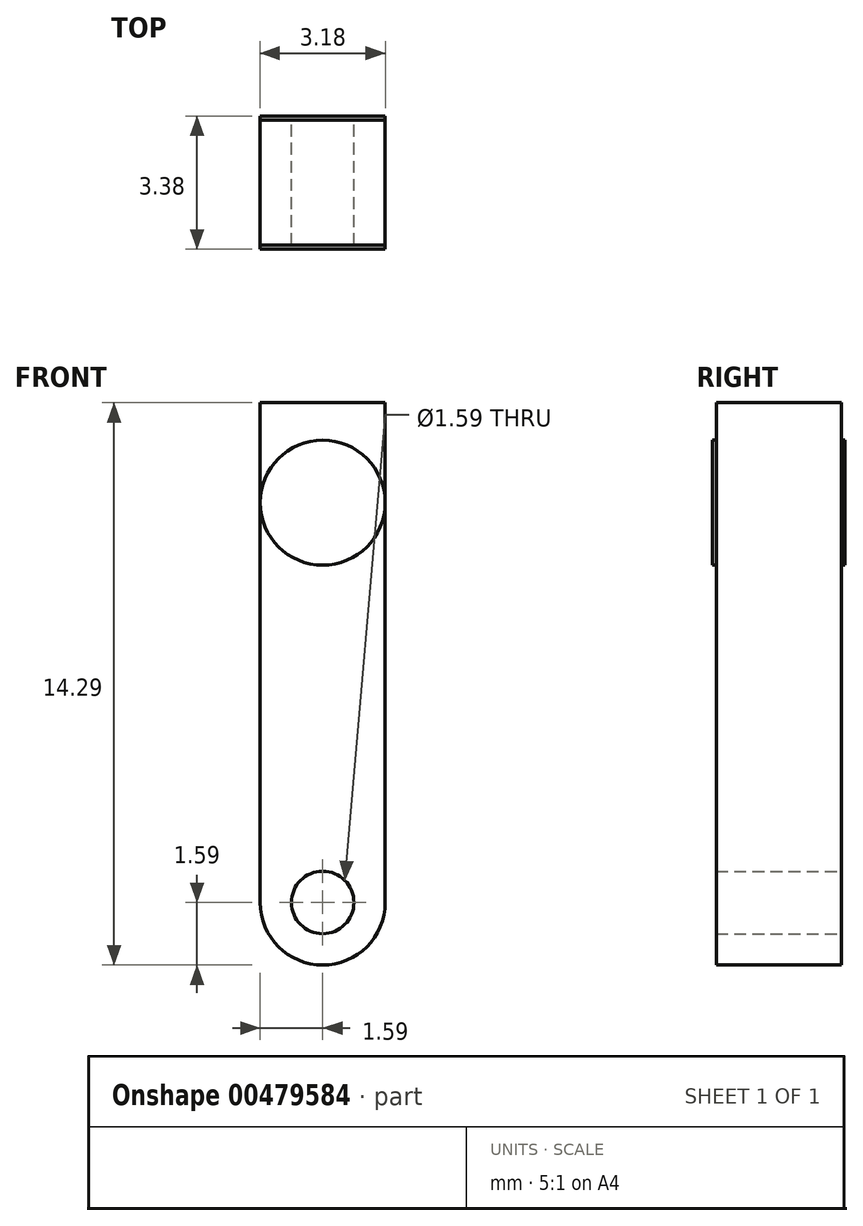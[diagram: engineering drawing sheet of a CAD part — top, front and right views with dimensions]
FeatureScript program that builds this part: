
annotation { "Feature Type Name" : "Feature", "Feature Type Description" : "" }
export const myFeature = defineFeature(function(context is Context, id is Id, definition is map)
    precondition{}
    {
        {
            var Q0;
            Q0=qCreatedBy(makeId("Front.planeOp"),FACE);
            var sketch = newSketch(context, id + "F0", { "sketchPlane" : qUnion([Q0])});
            skArc(sketch, "E0", {"start": v(-1.59, 0) * mm, "mid": v(0, -1.59) * mm, "end": v(1.59, 0) * mm});
            skLineSegment(sketch, "E1.bottom", {"start": v(-1.59, 0) * mm, "end": v(1.59, 0) * mm});
            skLineSegment(sketch, "E1.top", {"start": v(-1.59, 12.7) * mm, "end": v(1.59, 12.7) * mm});
            skLineSegment(sketch, "E1.left", {"start": v(-1.59, 0) * mm, "end": v(-1.59, 12.7) * mm});
            skLineSegment(sketch, "E1.right", {"start": v(1.59, 0) * mm, "end": v(1.59, 12.7) * mm});
            skCircle(sketch, "E2", {"center": v(0, 0) * mm, "radius": 0.8 * mm});
            skCircle(sketch, "E3", {"center": v(0, 10.16) * mm, "radius": 1.59 * mm});
            skSolve(sketch);
        }
        {
            var Q0;
            {var subQ1=sQuery(id+"F0.wireOp",EDGE,"E1.bottom");var subQ9=sQuery(id+"F0.wireOp",EDGE,"E2");var subQ11=makeQuery(id+"F0.imprint","INTERSECT",VERTEX,{"disambiguationData":[OD(0.0)],"derivedFrom":[subQ1,subQ9]});Q0=makeQuery(id+"F0.imprint","IMPRINT",FACE,{"disambiguationData":[TD([[makeQuery(id+"F0.imprint","IMPRINT",EDGE,{"disambiguationData":[TD([[subQ11,1.0]])],"derivedFrom":subQ9}),-1.0]])]});}
            var Q1;
            {var subQ0=sQuery(id+"F0.wireOp",EDGE,"E3");var subQ1=makeQuery(id+"F0.imprint","INTERSECT",VERTEX,{"derivedFrom":[sQuery(id+"F0.wireOp",EDGE,"E1.left"),subQ0]});Q1=makeQuery(id+"F0.imprint","IMPRINT",FACE,{"disambiguationData":[TD([[makeQuery(id+"F0.imprint","IMPRINT",EDGE,{"disambiguationData":[TD([[subQ1,1.0]])],"derivedFrom":subQ0}),1.0]])]});}
            var Q2;
            {var subQ0=sQuery(id+"F0.wireOp",EDGE,"E1.top");Q2=makeQuery(id+"F0.imprint","IMPRINT",FACE,{"disambiguationData":[TD([[makeQuery(id+"F0.imprint","IMPRINT",EDGE,{"derivedFrom":subQ0}),-1.0]])]});}
            var Q3;
            {var subQ0=sQuery(id+"F0.wireOp",EDGE,"E0");Q3=makeQuery(id+"F0.imprint","IMPRINT",FACE,{"disambiguationData":[TD([[makeQuery(id+"F0.imprint","IMPRINT",EDGE,{"derivedFrom":subQ0}),1.0]])]});}
            extrude(context, id + "F1", {"entities" : qUnion([Q0, Q1, Q2, Q3]), "depth" : 3.17 * mm, "symmetric" : true});
        }
        {
            var Q0;
            {var subQ0=sQuery(id+"F0.wireOp",EDGE,"E3");var subQ1=makeQuery(id+"F0.imprint","INTERSECT",VERTEX,{"derivedFrom":[sQuery(id+"F0.wireOp",EDGE,"E1.left"),subQ0]});Q0=makeQuery(id+"F0.imprint","IMPRINT",FACE,{"disambiguationData":[TD([[makeQuery(id+"F0.imprint","IMPRINT",EDGE,{"disambiguationData":[TD([[subQ1,1.0]])],"derivedFrom":subQ0}),1.0]])]});}
            extrude(context, id + "F2", {"entities" : qUnion([Q0]), "operationType" : NewBodyOperationType.ADD, "depth" : 3.37 * mm, "symmetric" : true});
        }
    });
